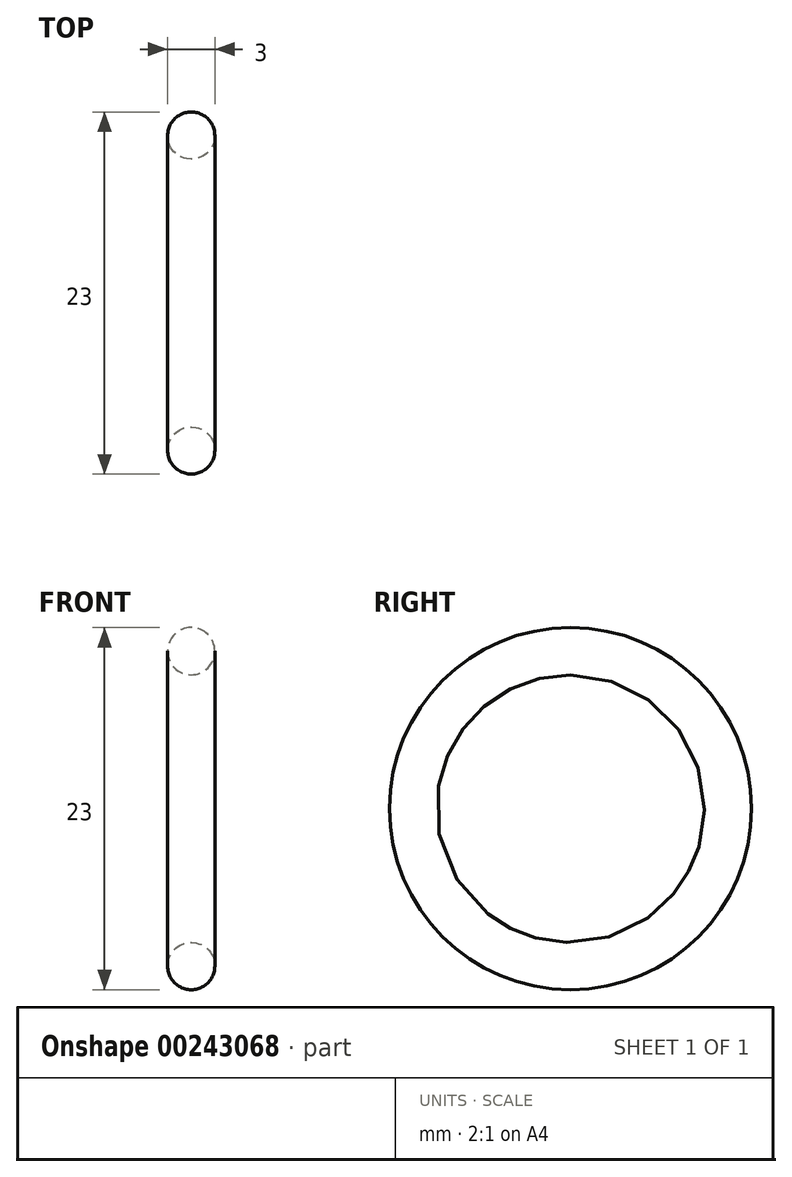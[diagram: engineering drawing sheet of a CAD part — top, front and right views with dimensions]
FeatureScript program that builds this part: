
annotation { "Feature Type Name" : "Feature", "Feature Type Description" : "" }
export const myFeature = defineFeature(function(context is Context, id is Id, definition is map)
    precondition{}
    {
        {
            var Q0;
            Q0=qCreatedBy(makeId("Front.planeOp"),FACE);
            var sketch = newSketch(context, id + "F0", { "sketchPlane" : qUnion([Q0])});
            skLineSegment(sketch, "E0", {"start": v(0, 0) * mm, "end": v(10, 0) * mm, "construction": true});
            skLineSegment(sketch, "E1", {"start": v(0, 0) * mm, "end": v(0, 10) * mm, "construction": true});
            skCircle(sketch, "E2", {"center": v(0, 10) * mm, "radius": 1.5 * mm});
            skCircle(sketch, "E3", {"center": v(10, 0) * mm, "radius": 1.5 * mm});
            skSolve(sketch);
        }
        {
            var Q0;
            Q0=makeQuery(id+"F0.imprint","IMPRINT",FACE,{"disambiguationData":[TD([[makeQuery(id+"F0.imprint","IMPRINT",EDGE,{"derivedFrom":sQuery(id+"F0.wireOp",EDGE,"E2")}),1.0]])]});
            var Q1;
            Q1=sQuery(id+"F0.wireOp",EDGE,"E0");
            revolve(context, id + "F1", {"entities" : qUnion([Q0]), "axis" : qUnion([Q1]), "revolveType" : RevolveType.FULL});
        }
        {
            var Q0;
            Q0=sQuery(id+"F0.wireOp",EDGE,"E3");
            var Q1;
            Q1=sQuery(id+"F0.wireOp",EDGE,"E1");
            revolve(context, id + "F2", {"bodyType" : ToolBodyType.SURFACE, "surfaceEntities" : qUnion([Q0]), "axis" : qUnion([Q1]), "revolveType" : RevolveType.FULL});
        }
    });
